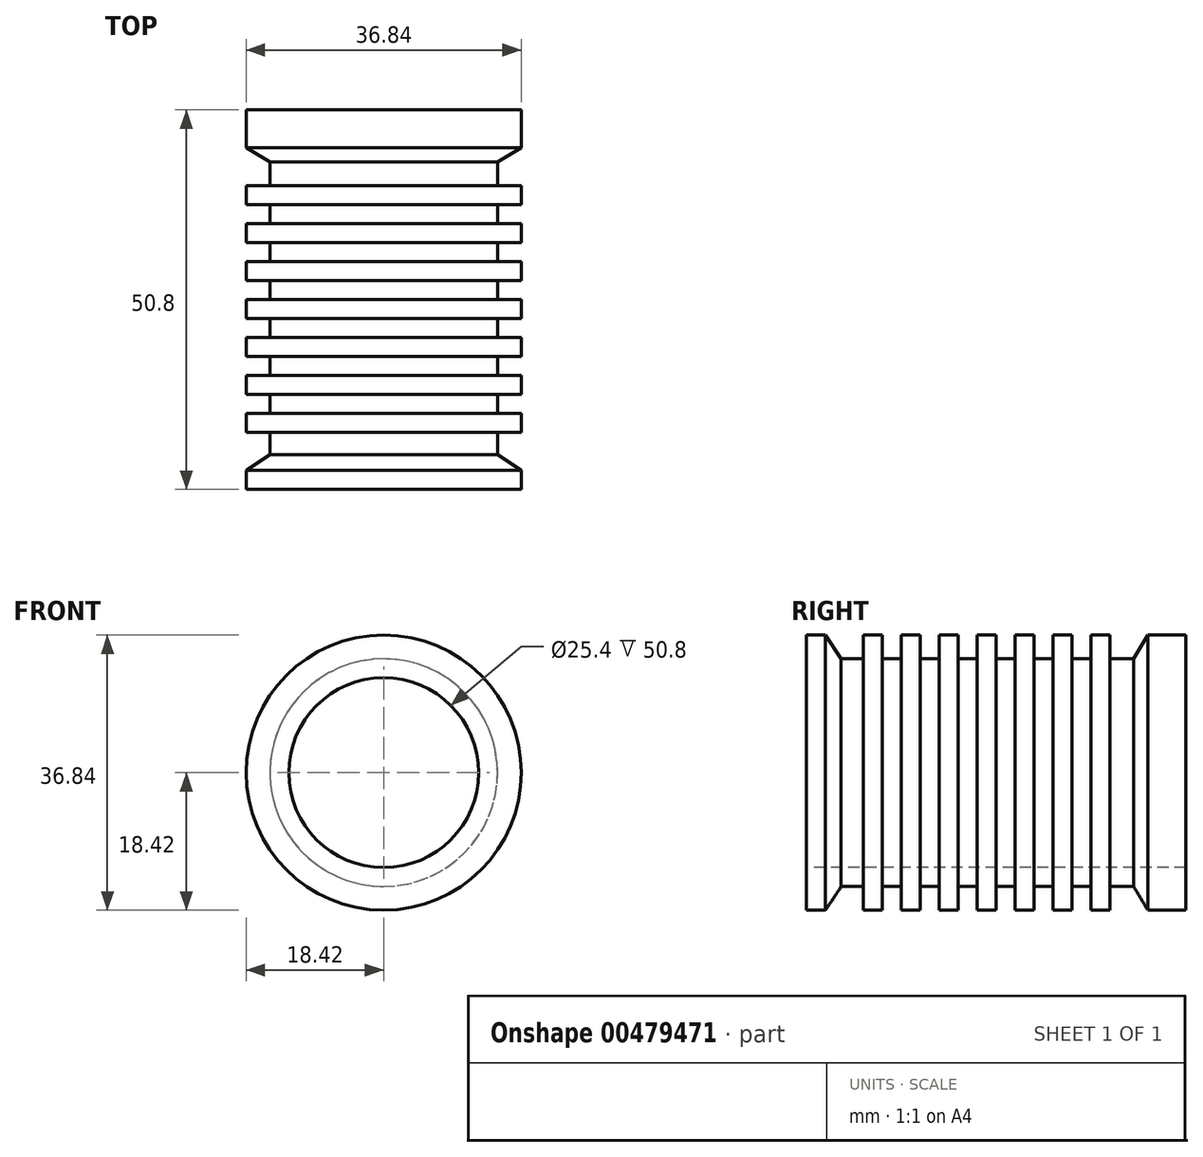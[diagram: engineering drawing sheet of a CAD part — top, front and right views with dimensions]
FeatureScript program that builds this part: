
annotation { "Feature Type Name" : "Feature", "Feature Type Description" : "" }
export const myFeature = defineFeature(function(context is Context, id is Id, definition is map)
    precondition{}
    {
        {
            var Q0;
            Q0=qCreatedBy(makeId("Front.planeOp"),FACE);
            var sketch = newSketch(context, id + "F0", { "sketchPlane" : qUnion([Q0])});
            skCircle(sketch, "E0", {"center": v(0, 0) * mm, "radius": 18.41 * mm});
            skCircle(sketch, "E1", {"center": v(0, 0) * mm, "radius": 12.7 * mm});
            skSolve(sketch);
        }
        {
            var Q0;
            Q0 = qSketchRegion(id + "F0", true);
            extrude(context, id + "F1", {"entities" : qUnion([Q0]), "oppositeDirection" : true, "depth" : 101.6 * mm, "offsetDistance" : 25.4 * mm, "hasSecondDirection" : true, "secondDirectionOppositeDirection" : true, "secondDirectionDepth" : 88.9 * mm});
        }
        {
            var Q0;
            Q0 = qSketchRegion(id + "F0", true);
            extrude(context, id + "F2", {"entities" : qUnion([Q0]), "operationType" : NewBodyOperationType.ADD, "oppositeDirection" : true, "depth" : 86.36 * mm, "offsetDistance" : 25.4 * mm, "hasSecondDirection" : true, "secondDirectionOppositeDirection" : true, "secondDirectionDepth" : 83.82 * mm});
        }
        {
            var Q0;
            Q0 = qSketchRegion(id + "F0", true);
            extrude(context, id + "F3", {"entities" : qUnion([Q0]), "operationType" : NewBodyOperationType.ADD, "oppositeDirection" : true, "depth" : 81.28 * mm, "offsetDistance" : 25.4 * mm, "hasSecondDirection" : true, "secondDirectionOppositeDirection" : true, "secondDirectionDepth" : 78.74 * mm});
        }
        {
            var Q0;
            Q0 = qSketchRegion(id + "F0", true);
            extrude(context, id + "F4", {"entities" : qUnion([Q0]), "operationType" : NewBodyOperationType.ADD, "oppositeDirection" : true, "depth" : 76.2 * mm, "offsetDistance" : 25.4 * mm, "hasSecondDirection" : true, "secondDirectionOppositeDirection" : true, "secondDirectionDepth" : 73.66 * mm});
        }
        {
            var Q0;
            Q0 = qSketchRegion(id + "F0", true);
            extrude(context, id + "F5", {"entities" : qUnion([Q0]), "operationType" : NewBodyOperationType.ADD, "oppositeDirection" : true, "depth" : 71.12 * mm, "offsetDistance" : 25.4 * mm, "hasSecondDirection" : true, "secondDirectionOppositeDirection" : true, "secondDirectionDepth" : 68.58 * mm});
        }
        {
            var Q0;
            Q0 = qSketchRegion(id + "F0", true);
            var Q1;
            Q1 = qConstructionFilter(qBodyType(qCreatedBy(id + "F0" ,EDGE), BodyType.WIRE), ConstructionObject.NO);
            extrude(context, id + "F6", {"entities" : qUnion([Q0]), "operationType" : NewBodyOperationType.ADD, "surfaceEntities" : qUnion([Q1]), "oppositeDirection" : true, "depth" : 66.04 * mm, "offsetDistance" : 25.4 * mm, "hasSecondDirection" : true, "secondDirectionOppositeDirection" : true, "secondDirectionDepth" : 63.5 * mm});
        }
        {
            var Q0;
            Q0 = qSketchRegion(id + "F0", true);
            extrude(context, id + "F7", {"entities" : qUnion([Q0]), "operationType" : NewBodyOperationType.ADD, "oppositeDirection" : true, "depth" : 60.96 * mm, "offsetDistance" : 25.4 * mm, "hasSecondDirection" : true, "secondDirectionOppositeDirection" : true, "secondDirectionDepth" : 58.42 * mm});
        }
        {
            var Q0;
            Q0 = qSketchRegion(id + "F0", true);
            extrude(context, id + "F8", {"entities" : qUnion([Q0]), "operationType" : NewBodyOperationType.ADD, "oppositeDirection" : true, "depth" : 55.88 * mm, "offsetDistance" : 25.4 * mm});
        }
        {
            var Q0;
            Q0=qCreatedBy(makeId("Front.planeOp"),FACE);
            var sketch = newSketch(context, id + "F9", { "sketchPlane" : qUnion([Q0])});
            skCircle(sketch, "E2", {"center": v(0, 0) * mm, "radius": 15.24 * mm});
            skCircle(sketch, "E3", {"center": v(0, 0) * mm, "radius": 12.7 * mm});
            skSolve(sketch);
        }
        {
            var Q0;
            Q0 = qSketchRegion(id + "F9", true);
            extrude(context, id + "F10", {"entities" : qUnion([Q0]), "operationType" : NewBodyOperationType.ADD, "oppositeDirection" : true, "depth" : 101.6 * mm, "offsetDistance" : 25.4 * mm});
        }
        {
            var Q0;
            Q0=makeQuery(id+"F8.opExtrude","CAP_EDGE",EDGE,{"disambiguationData":[OSD([sQuery(id+"F0.wireOp",EDGE,"E0")])],"isStart":false});
            chamfer(context, id + "F11", {"entities" : qUnion([Q0]), "chamferType" : ChamferType.TWO_OFFSETS, "width1" : 2.54 * mm, "oppositeDirection" : false, "width2" : 3.8 * mm, "tangentPropagation" : true});
        }
        {
            var Q0;
            Q0=makeQuery(id+"F1.opExtrude","CAP_EDGE",EDGE,{"disambiguationData":[OSD([sQuery(id+"F0.wireOp",EDGE,"E0")])],"isStart":true});
            chamfer(context, id + "F12", {"entities" : qUnion([Q0]), "chamferType" : ChamferType.TWO_OFFSETS, "width1" : 12.7 * mm, "oppositeDirection" : false, "width2" : 7.62 * mm, "tangentPropagation" : true});
        }
        {
            var Q0;
            Q0 = qSketchRegion(id + "F0", true);
            extrude(context, id + "F13", {"entities" : qUnion([Q0]), "operationType" : NewBodyOperationType.ADD, "oppositeDirection" : true, "depth" : 91.44 * mm, "offsetDistance" : 25.4 * mm, "hasSecondDirection" : true, "secondDirectionOppositeDirection" : true, "secondDirectionDepth" : 88.9 * mm});
        }
        {
            var Q0;
            Q0 = qSketchRegion(id + "F0", true);
            extrude(context, id + "F14", {"entities" : qUnion([Q0]), "operationType" : NewBodyOperationType.REMOVE, "oppositeDirection" : true, "depth" : 50.8 * mm, "offsetDistance" : 25.4 * mm});
        }
    });
